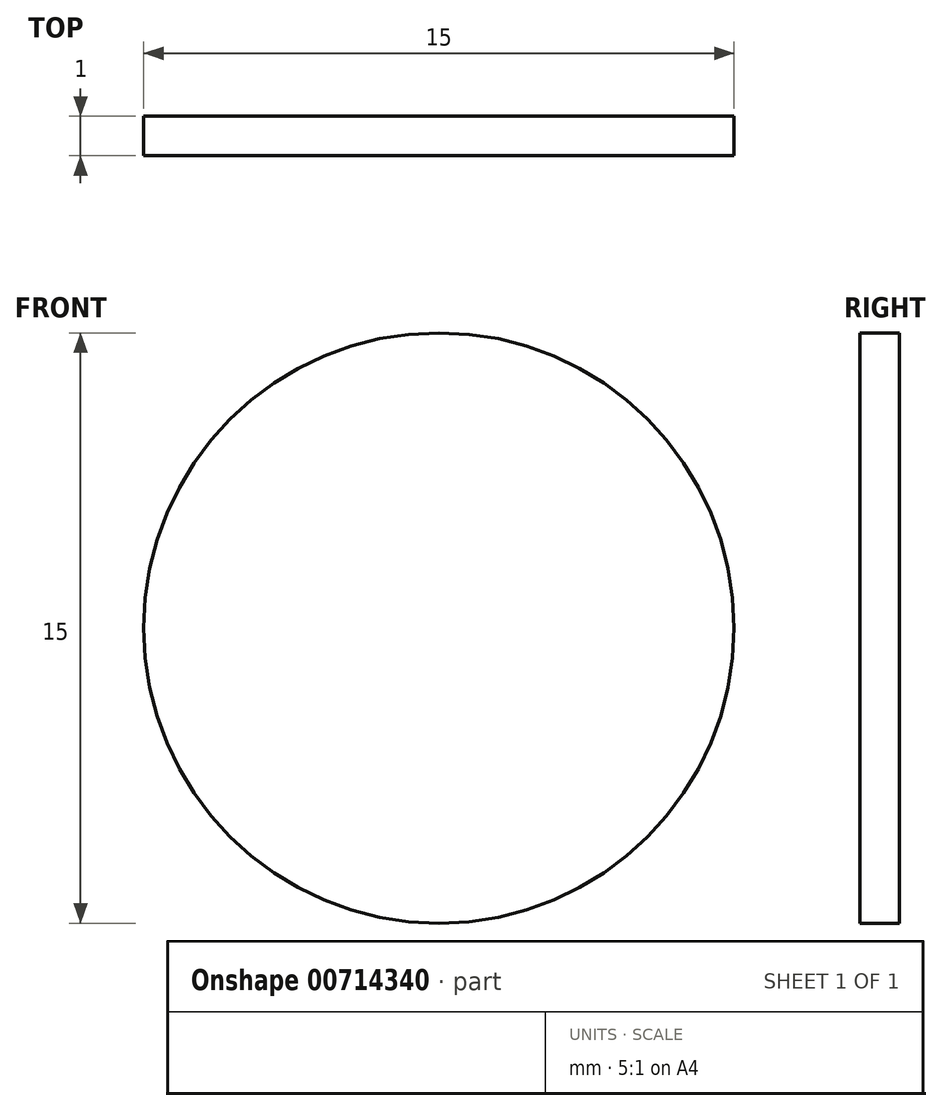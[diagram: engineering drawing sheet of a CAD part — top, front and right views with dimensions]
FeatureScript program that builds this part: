
annotation { "Feature Type Name" : "Feature", "Feature Type Description" : "" }
export const myFeature = defineFeature(function(context is Context, id is Id, definition is map)
    precondition{}
    {
        {
            var Q0;
            Q0=qCreatedBy(makeId("Front.planeOp"),FACE);
            var sketch = newSketch(context, id + "F0", { "sketchPlane" : qUnion([Q0])});
            skCircle(sketch, "E0", {"center": v(0, 0) * mm, "radius": 7.5 * mm});
            skSolve(sketch);
        }
        {
            var Q0;
            Q0 = qSketchRegion(id + "F0", true);
            extrude(context, id + "F1", {"entities" : qUnion([Q0]), "depth" : 1 * mm, "offsetDistance" : 25 * mm});
        }
    });
